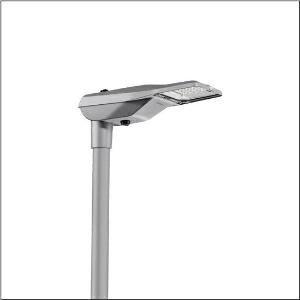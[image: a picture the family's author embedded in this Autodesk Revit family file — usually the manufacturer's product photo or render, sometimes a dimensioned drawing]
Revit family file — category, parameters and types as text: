
# Revit family: streetlight_sl_21_iq_micro___st1_0a_5xe1d31y08cb_1c09
name_source: partatom
category: Lighting Fixtures
units: mm (PartAtom-declared; Revit-internal decimal feet)

## family parameters
Cut with Voids When Loaded = No
Host = Face
Light Source = No
Part Type = Normal
Room Calculation Point = No
Round Connector Dimension = Use Diameter
Shared = No

## types (1)
- --- (1 x LED, 2880 lm, 19.1 W, 3000K)
    Apparent Load = 19 VA
    CIE Flux Codes = 37 72 97 100 100
    Color Rendering = 70
    Color Temperature = 3000K
    Default Elevation = 1800 mm
    Description = Streetlight SL 21 iQ micro, mast luminaire, primary light control with lens, of PMMA, primary optical cover: cover, of toughened safety glass, transparent, light distribution: ST1.0a, light emission: direct distribution, primary light characteristic: asymmetric, installation type: post-top, side-entry, LED, High Power LED, rated luminous flux: 2.880lm, luminous efficacy: 151lm/W, light colour: 730, colour temperature: 3000K, control: presetting dimming logarithmic, Street-Remote, Auto-Match, Temp-Guard, Lumen-Switch, Night-Set, Smart-Wire, Light-Fading, Desk-Remote (wireless, voltage-free reading and setting of iQ features in the workshop via application-optimized NFC function/RFID function), optimised constant luminous flux control (CLO 2.0), mains connection: 220..240V, AC, 50/60Hz, start of lifetime: 19W, end of service life: 20W, reduction: 9W, luminaire housing, of diecast aluminium, powder-coated, Siteco® metallic grey (DB 702S), corrosivity category C5 mid according to DIN EN ISO 12944, please order mast flange separately, inclination adjustable: 0°, 5°, 10°, 15°, sealing non-destructively replaceable, multi-level sealing system, length: 528mm, width: 235mm, height: 110mm, mast flange for spigot size: 42mm (side-entry): 5XC10008XM4, 60/48mm (side-entry/post-top): 5XC10108XM2, 76/60mm (side-entry/post-top): 5XC10108XM1, Smart Interface below and above, protection rating (complete): IP66, insulation class (complete): insulation class II (safety insulation), certification: CE, ENEC, ENEC+, VDE, impact resistance: IK09, permissible operating ambient temperature for outdoor applications: -40..+50°C, standard-compliant lighting for roads and squares, packaging unit: 1 piece

Light Distribution: ST1.0a
    Height = 110 mm
    Lamp = 1 x LED
    Lamp Light Flux = 2880 lm
    Lamp Power = 19.1 W
    Lamp count = 1
    Length = 528 mm
    Luminous efficacy = 151 lm/W
    Manufacturer = Siteco
    ModVariant = No
    Model = 5XE1D31Y08CB
    Number of Poles = 1
    OnlyDefault = Yes
    Power Factor = 1
    Product Name = Streetlight SL 21 iQ micro | ST1.0a
    Product group = mast luminaire | pylon top
    ProductGroupID = 6100
    Protection Class = Protection class II
    Protection Degree = IP 66
    RLX_Detail_Level = 1
    RLX_Emergency_Light_Flux = 0 lm
    RLX_Emergency_Type = 0
    RLX_Emergency_Type_DB = No
    RlxData = <blob elided: 98393 chars, md5=53c95c17>
    Socket = socket
    Standby Power = 0 W
    System Light Flux = 2880 lm
    System Power = 19 W
    Type Comments = factory setting: luminous flux: 100 % | dim-lin: 254 | 387 mA
    Type Image = l_1007239.jpg
    URL = http://relux.com
    VarID = @adj_045495
    Voltage = 0 V
    Weight = 0.00 kg
    Width = 235 mm

## geometry (parser evidence)
native form markers: Blend x4, Sweep x12
no freeform markers — native parametric forms only
